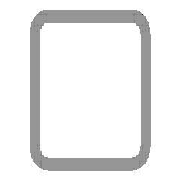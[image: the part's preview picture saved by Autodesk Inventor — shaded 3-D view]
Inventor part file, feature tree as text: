
AUTODESK INVENTOR PART (.ipt)
format: ipt  version: 2025 (Build 290162010, 162A)  size: 135,168 bytes
history: native  units: mm (DEFAULTED — no unit token found)
features: other x4, sketch x1, plane x1
ambient origin geometry x8: Origin, YZ Plane, XZ Plane, XY Plane, X Axis, Y Axis, Z Axis, Center Point
bodies: Solid1 (feature_tree), Body (feature_tree)
feature tree (6):
  parser-record x1  (decoder bookkeeping rows leaked as tree rows — omitted from the tree; the rows remain in map.json)
  other  "Driven Length"
  other  "Start plane"
  other  "End plane"
  sketch  "Sketch3"  dims[d3=2800.0mm d4=0.0mm d7=6.0mm d9=80.0mm d11=80.0mm d12=3.0mm d13=-0.0mm d14=2800.0mm d15=40.0mm d16=40.0mm d17=90.0deg d18=2800.0mm]
  plane  "Work Plane3"
